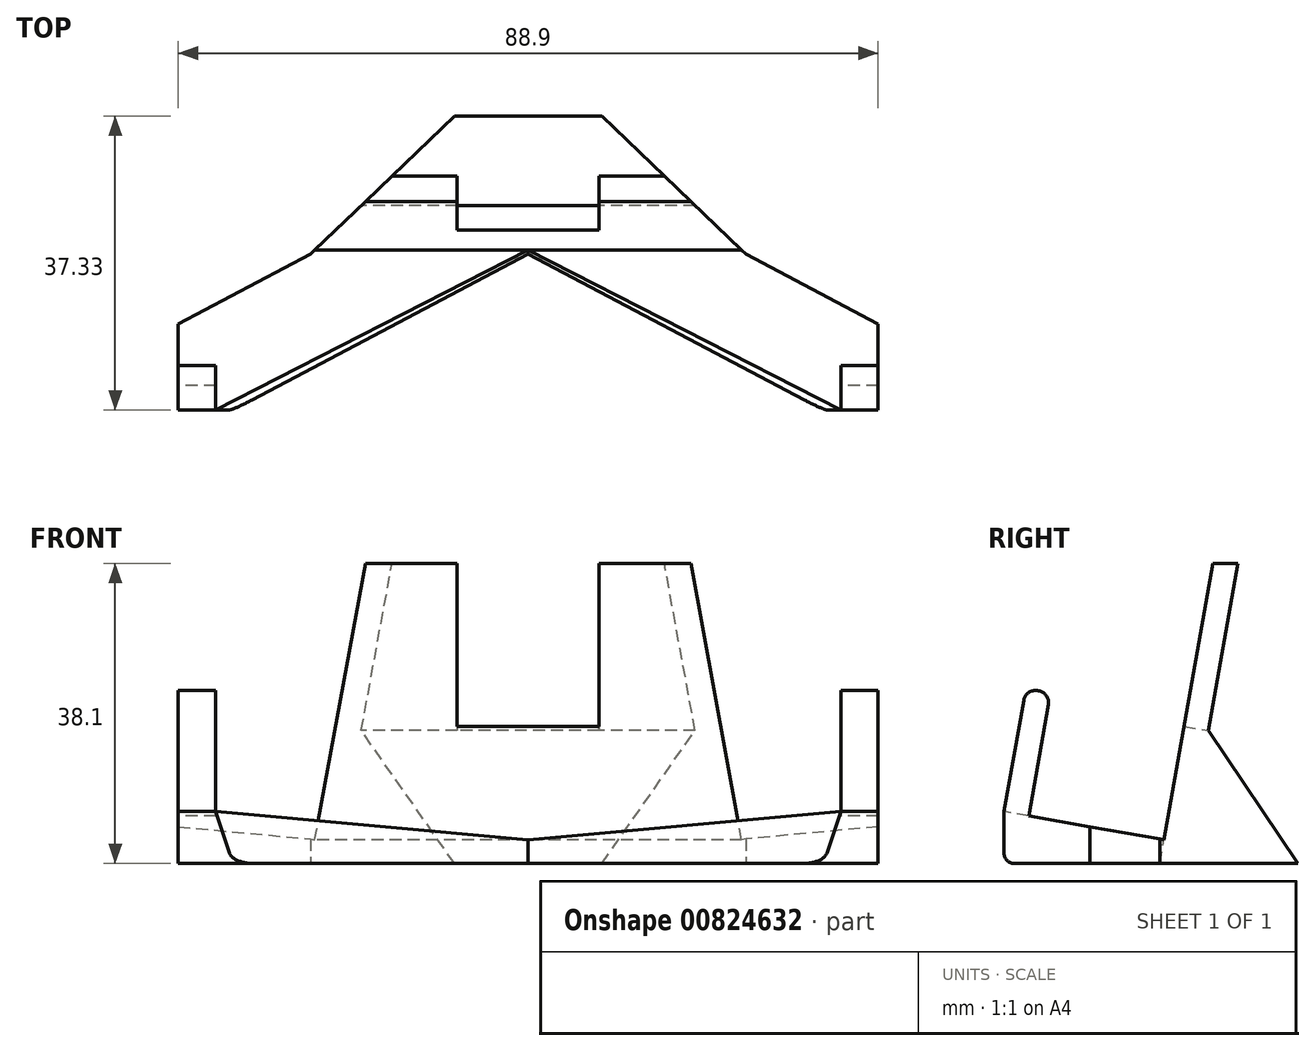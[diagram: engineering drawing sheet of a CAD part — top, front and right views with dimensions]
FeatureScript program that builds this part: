
annotation { "Feature Type Name" : "Feature", "Feature Type Description" : "" }
export const myFeature = defineFeature(function(context is Context, id is Id, definition is map)
    precondition{}
    {
        {
            var Q0;
            Q0=qCreatedBy(makeId("Front.planeOp"),FACE);
            var sketch = newSketch(context, id + "F0", { "sketchPlane" : qUnion([Q0])});
            skLineSegment(sketch, "E0.bottom", {"start": v(0, 0) * mm, "end": v(88.9, 0) * mm});
            skLineSegment(sketch, "E0.top", {"start": v(0, 38.1) * mm, "end": v(88.9, 38.1) * mm});
            skLineSegment(sketch, "E0.left", {"start": v(0, 0) * mm, "end": v(0, 38.1) * mm});
            skLineSegment(sketch, "E0.right", {"start": v(88.9, 0) * mm, "end": v(88.9, 38.1) * mm});
            skSolve(sketch);
        }
        {
            var Q0;
            Q0=makeQuery(id+"F0.imprint","IMPRINT",FACE,{"disambiguationData":[TD([[makeQuery(id+"F0.imprint","IMPRINT",EDGE,{"derivedFrom":sQuery(id+"F0.wireOp",EDGE,"E0.bottom")}),1.0]])]});
            extrude(context, id + "F1", {"entities" : qUnion([Q0]), "depth" : 42.85 * mm, "offsetDistance" : 25.4 * mm});
        }
        {
            var Q0;
            Q0=makeQuery(id+"F1.opExtrude","SWEPT_FACE",FACE,{"disambiguationData":[OSD([sQuery(id+"F0.wireOp",EDGE,"E0.left")])]});
            var sketch = newSketch(context, id + "F2", { "sketchPlane" : qUnion([Q0])});
            skLineSegment(sketch, "E1", {"start": v(22.54, 3) * mm, "end": v(39.72, 6.03) * mm});
            skLineSegment(sketch, "E2", {"start": v(42.85, 6.58) * mm, "end": v(40.1, 22.22) * mm});
            skLineSegment(sketch, "E3", {"start": v(39.72, 6.03) * mm, "end": v(36.97, 21.67) * mm});
            skLineSegment(sketch, "E4", {"start": v(36.97, 21.67) * mm, "end": v(40.1, 22.22) * mm});
            skLineSegment(sketch, "E5", {"start": v(16.35, 38.1) * mm, "end": v(22.54, 3) * mm});
            skLineSegment(sketch, "E6", {"start": v(13.13, 38.1) * mm, "end": v(16.87, 16.87) * mm});
            skLineSegment(sketch, "E7", {"start": v(16.87, 16.87) * mm, "end": v(5.52, 0) * mm});
            skPoint(sketch, "E8.start.orphan", {"position": v(23.8, 0) * mm});
            skSolve(sketch);
        }
        {
            var Q0;
            {var subQ4=sQuery(id+"F2.wireOp",EDGE,"E6");Q0=makeQuery(id+"F2.imprint","IMPRINT",FACE,{"disambiguationData":[TD([[makeQuery(id+"F2.imprint","IMPRINT",EDGE,{"derivedFrom":subQ4}),-1.0]])]});}
            var Q1;
            Q1=makeQuery(id+"F2.imprint","IMPRINT",FACE,{"disambiguationData":[TD([[makeQuery(id+"F2.imprint","IMPRINT",EDGE,{"derivedFrom":sQuery(id+"F2.wireOp",EDGE,"E1")}),1.0]])]});
            extrude(context, id + "F3", {"entities" : qUnion([Q0, Q1]), "operationType" : NewBodyOperationType.REMOVE, "oppositeDirection" : true, "depth" : 127 * mm, "offsetDistance" : 25.4 * mm});
        }
        {
            var Q0;
            Q0=makeQuery(id+"F3.boolean.opBoolean","COPY",FACE,{"derivedFrom":makeQuery(id+"F3.opExtrude","SWEPT_FACE",FACE,{"disambiguationData":[OSD([sQuery(id+"F2.wireOp",EDGE,"E2")])]})});
            var sketch = newSketch(context, id + "F4", { "sketchPlane" : qUnion([Q0])});
            skLineSegment(sketch, "E9.bottom", {"start": v(4.75, 14.92) * mm, "end": v(84.15, 14.92) * mm});
            skLineSegment(sketch, "E9.top", {"start": v(4.75, -0.96) * mm, "end": v(84.15, -0.96) * mm});
            skLineSegment(sketch, "E9.left", {"start": v(4.75, 14.92) * mm, "end": v(4.75, -0.96) * mm});
            skLineSegment(sketch, "E9.right", {"start": v(84.15, 14.92) * mm, "end": v(84.15, -0.96) * mm});
            skSolve(sketch);
        }
        {
            var Q0;
            Q0=makeQuery(id+"F4.imprint","IMPRINT",FACE,{"disambiguationData":[TD([[makeQuery(id+"F4.imprint","IMPRINT",EDGE,{"derivedFrom":sQuery(id+"F4.wireOp",EDGE,"E9.bottom")}),1.0]])]});
            extrude(context, id + "F5", {"entities" : qUnion([Q0]), "operationType" : NewBodyOperationType.REMOVE, "oppositeDirection" : true, "depth" : 6.35 * mm, "offsetDistance" : 25.4 * mm});
        }
        {
            var Q0;
            Q0=makeQuery(id+"F5.boolean.opBoolean","MERGE",FACE,{"derivedFrom":[makeQuery(id+"F3.boolean.opBoolean","COPY",FACE,{"derivedFrom":makeQuery(id+"F3.opExtrude","SWEPT_FACE",FACE,{"disambiguationData":[OSD([sQuery(id+"F2.wireOp",EDGE,"E1")])]})}),makeQuery(id+"F5.opExtrude","SWEPT_FACE",FACE,{"disambiguationData":[OSD([sQuery(id+"F4.wireOp",EDGE,"E9.top")])]})]});
            var sketch = newSketch(context, id + "F6", { "sketchPlane" : qUnion([Q0])});
            skLineSegment(sketch, "E10", {"start": v(0, -22.72) * mm, "end": v(88.9, -22.72) * mm});
            skLineSegment(sketch, "E11", {"start": v(4.75, -43.34) * mm, "end": v(44.45, -22.72) * mm});
            skLineSegment(sketch, "E12", {"start": v(84.15, -43.34) * mm, "end": v(44.45, -22.72) * mm});
            skLineSegment(sketch, "E13", {"start": v(0, -31.44) * mm, "end": v(16.8, -22.72) * mm});
            skLineSegment(sketch, "E14", {"start": v(88.9, -31.44) * mm, "end": v(72.1, -22.72) * mm});
            skSolve(sketch);
        }
        {
            var Q0;
            {var subQ3=sQuery(id+"F6.wireOp",EDGE,"E13");Q0=makeQuery(id+"F6.imprint","IMPRINT",FACE,{"disambiguationData":[TD([[makeQuery(id+"F6.imprint","IMPRINT",EDGE,{"derivedFrom":subQ3}),1.0]])]});}
            var Q1;
            Q1=makeQuery(id+"F6.imprint","IMPRINT",FACE,{"disambiguationData":[TD([[makeQuery(id+"F6.imprint","IMPRINT",EDGE,{"derivedFrom":sQuery(id+"F6.wireOp",EDGE,"E11")}),-1.0]])]});
            var Q2;
            {var subQ3=sQuery(id+"F6.wireOp",EDGE,"E14");Q2=makeQuery(id+"F6.imprint","IMPRINT",FACE,{"disambiguationData":[TD([[makeQuery(id+"F6.imprint","IMPRINT",EDGE,{"derivedFrom":subQ3}),-1.0]])]});}
            extrude(context, id + "F7", {"entities" : qUnion([Q0, Q1, Q2]), "operationType" : NewBodyOperationType.REMOVE, "oppositeDirection" : true, "depth" : 25.4 * mm, "offsetDistance" : 25.4 * mm});
        }
        {
            var Q0;
            Q0=makeQuery(id+"F1.opExtrude","SWEPT_FACE",FACE,{"disambiguationData":[OSD([sQuery(id+"F0.wireOp",EDGE,"E0.bottom")])]});
            var sketch = newSketch(context, id + "F8", { "sketchPlane" : qUnion([Q0])});
            skLineSegment(sketch, "E15", {"start": v(44.45, 5.52) * mm, "end": v(44.45, -5.42) * mm});
            skPoint(sketch, "E15.endSnap0", {"position": v(44.45, 5.52) * mm});
            skLineSegment(sketch, "E16", {"start": v(16.8, 23.07) * mm, "end": v(35.08, 5.52) * mm});
            skLineSegment(sketch, "E17", {"start": v(72.1, 23.07) * mm, "end": v(53.82, 5.52) * mm});
            skPoint(sketch, "E18.start.orphan", {"position": v(25.7, 32.96) * mm});
            skPoint(sketch, "E19.start.orphan", {"position": v(63.2, 32.96) * mm});
            skSolve(sketch);
        }
        {
            var Q0;
            {var subQ0=sQuery(id+"F8.wireOp",EDGE,"E16");Q0=makeQuery(id+"F8.imprint","IMPRINT",FACE,{"disambiguationData":[TD([[makeQuery(id+"F8.imprint","IMPRINT",EDGE,{"derivedFrom":subQ0}),-1.0]])]});}
            var Q1;
            {var subQ0=sQuery(id+"F8.wireOp",EDGE,"E17");Q1=makeQuery(id+"F8.imprint","IMPRINT",FACE,{"disambiguationData":[TD([[makeQuery(id+"F8.imprint","IMPRINT",EDGE,{"derivedFrom":subQ0}),1.0]])]});}
            extrude(context, id + "F9", {"entities" : qUnion([Q0, Q1]), "operationType" : NewBodyOperationType.REMOVE, "oppositeDirection" : true, "depth" : 127 * mm, "offsetDistance" : 25.4 * mm});
        }
        {
            var Q0;
            Q0=makeQuery(id+"F3.boolean.opBoolean","COPY",EDGE,{"derivedFrom":makeQuery(id+"F3.opExtrude","SWEPT_EDGE",EDGE,{"disambiguationData":[OSD([sQuery(id+"F0.wireOp",EDGE,"E0.top"),sQuery(id+"F0.wireOp",EDGE,"E0.left"),sQuery(id+"F2.wireOp",EDGE,"E6")])]})});
            var Q1;
            Q1=makeQuery(id+"F3.boolean.opBoolean","COPY",EDGE,{"derivedFrom":makeQuery(id+"F3.opExtrude","SWEPT_EDGE",EDGE,{"disambiguationData":[OSD([sQuery(id+"F0.wireOp",EDGE,"E0.top"),sQuery(id+"F0.wireOp",EDGE,"E0.left"),sQuery(id+"F2.wireOp",EDGE,"E5")])]})});
            var Q2;
            {var subQ0=sQuery(id+"F2.wireOp",EDGE,"E3");var subQ1=sQuery(id+"F2.wireOp",EDGE,"E4");Q2=makeQuery(id+"F5.boolean.opBoolean","SPLIT",EDGE,{"disambiguationData":[TD([makeQuery(id+"F1.opExtrude","SWEPT_FACE",FACE,{"disambiguationData":[OSD([sQuery(id+"F0.wireOp",EDGE,"E0.left")])]})])],"derivedFrom":makeQuery(id+"F3.boolean.opBoolean","COPY",EDGE,{"derivedFrom":makeQuery(id+"F3.opExtrude","SWEPT_EDGE",EDGE,{"disambiguationData":[OSD([subQ0,subQ1])]})})});}
            var Q3;
            {var subQ0=sQuery(id+"F2.wireOp",EDGE,"E2");var subQ1=sQuery(id+"F2.wireOp",EDGE,"E4");Q3=makeQuery(id+"F5.boolean.opBoolean","SPLIT",EDGE,{"disambiguationData":[TD([makeQuery(id+"F1.opExtrude","SWEPT_FACE",FACE,{"disambiguationData":[OSD([sQuery(id+"F0.wireOp",EDGE,"E0.left")])]})])],"derivedFrom":makeQuery(id+"F3.boolean.opBoolean","COPY",EDGE,{"derivedFrom":makeQuery(id+"F3.opExtrude","SWEPT_EDGE",EDGE,{"disambiguationData":[OSD([subQ0,subQ1])]})})});}
            var Q4;
            {var subQ0=sQuery(id+"F2.wireOp",EDGE,"E3");var subQ1=sQuery(id+"F2.wireOp",EDGE,"E4");Q4=makeQuery(id+"F5.boolean.opBoolean","SPLIT",EDGE,{"disambiguationData":[TD([makeQuery(id+"F1.opExtrude","SWEPT_FACE",FACE,{"disambiguationData":[OSD([sQuery(id+"F0.wireOp",EDGE,"E0.right")])]})])],"derivedFrom":makeQuery(id+"F3.boolean.opBoolean","COPY",EDGE,{"derivedFrom":makeQuery(id+"F3.opExtrude","SWEPT_EDGE",EDGE,{"disambiguationData":[OSD([subQ0,subQ1])]})})});}
            var Q5;
            {var subQ0=sQuery(id+"F2.wireOp",EDGE,"E2");var subQ1=sQuery(id+"F2.wireOp",EDGE,"E4");Q5=makeQuery(id+"F5.boolean.opBoolean","SPLIT",EDGE,{"disambiguationData":[TD([makeQuery(id+"F1.opExtrude","SWEPT_FACE",FACE,{"disambiguationData":[OSD([sQuery(id+"F0.wireOp",EDGE,"E0.right")])]})])],"derivedFrom":makeQuery(id+"F3.boolean.opBoolean","COPY",EDGE,{"derivedFrom":makeQuery(id+"F3.opExtrude","SWEPT_EDGE",EDGE,{"disambiguationData":[OSD([subQ0,subQ1])]})})});}
            fillet(context, id + "F10", {"entities" : qUnion([Q0, Q1, Q2, Q3, Q4, Q5]), "radius" : 1.52 * mm, "tangentPropagation" : true, "allowEdgeOverflow" : false});
        }
        {
            var Q0;
            Q0=makeQuery(id+"F1.opExtrude","SWEPT_FACE",FACE,{"disambiguationData":[OSD([sQuery(id+"F0.wireOp",EDGE,"E0.bottom")])]});
            var sketch = newSketch(context, id + "F11", { "sketchPlane" : qUnion([Q0])});
            skLineSegment(sketch, "E20", {"start": v(0, 31.93) * mm, "end": v(16.8, 23.07) * mm});
            skLineSegment(sketch, "E21", {"start": v(16.8, 23.07) * mm, "end": v(16.1, 21.75) * mm});
            skLineSegment(sketch, "E22", {"start": v(16.1, 21.75) * mm, "end": v(0, 30.78) * mm});
            skLineSegment(sketch, "E23", {"start": v(0, 30.78) * mm, "end": v(0, 31.93) * mm});
            skLineSegment(sketch, "E24", {"start": v(72.1, 23.07) * mm, "end": v(72.6, 22.13) * mm});
            skLineSegment(sketch, "E25", {"start": v(72.6, 22.13) * mm, "end": v(88.9, 30.41) * mm});
            skLineSegment(sketch, "E26", {"start": v(88.9, 30.41) * mm, "end": v(88.9, 31.93) * mm});
            skLineSegment(sketch, "E27", {"start": v(88.9, 31.93) * mm, "end": v(72.1, 23.07) * mm});
            skSolve(sketch);
        }
        {
            var Q0;
            Q0=makeQuery(id+"F11.imprint","IMPRINT",FACE,{"disambiguationData":[TD([[makeQuery(id+"F11.imprint","IMPRINT",EDGE,{"derivedFrom":sQuery(id+"F11.wireOp",EDGE,"E20")}),-1.0]])]});
            var Q1;
            Q1=makeQuery(id+"F11.imprint","IMPRINT",FACE,{"disambiguationData":[TD([[makeQuery(id+"F11.imprint","IMPRINT",EDGE,{"derivedFrom":sQuery(id+"F11.wireOp",EDGE,"E24")}),1.0]])]});
            extrude(context, id + "F12", {"entities" : qUnion([Q0, Q1]), "operationType" : NewBodyOperationType.REMOVE, "oppositeDirection" : true, "depth" : 25.4 * mm, "offsetDistance" : 25.4 * mm});
        }
        {
            var Q0;
            Q0=makeQuery(id+"F3.boolean.opBoolean","COPY",EDGE,{"derivedFrom":makeQuery(id+"F3.opExtrude","SWEPT_EDGE",EDGE,{"disambiguationData":[OSD([sQuery(id+"F0.wireOp",EDGE,"E0.bottom"),sQuery(id+"F0.wireOp",EDGE,"E0.left"),sQuery(id+"F2.wireOp",EDGE,"E7")])]})});
            var Q1;
            {var subQ0=sQuery(id+"F0.wireOp",EDGE,"E0.bottom");var subQ1=sQuery(id+"F0.wireOp",EDGE,"E0.right");Q1=makeQuery(id+"F7.boolean.opBoolean","SPLIT",EDGE,{"disambiguationData":[TD([makeQuery(id+"F1.opExtrude","SWEPT_FACE",FACE,{"disambiguationData":[OSD([subQ1])]})])],"derivedFrom":makeQuery(id+"F1.opExtrude","CAP_EDGE",EDGE,{"disambiguationData":[OSD([subQ0])],"isStart":false})});}
            var Q2;
            {var subQ0=sQuery(id+"F0.wireOp",EDGE,"E0.bottom");var subQ1=sQuery(id+"F0.wireOp",EDGE,"E0.left");Q2=makeQuery(id+"F7.boolean.opBoolean","SPLIT",EDGE,{"disambiguationData":[TD([makeQuery(id+"F1.opExtrude","SWEPT_FACE",FACE,{"disambiguationData":[OSD([subQ1])]})])],"derivedFrom":makeQuery(id+"F1.opExtrude","CAP_EDGE",EDGE,{"disambiguationData":[OSD([subQ0])],"isStart":false})});}
            fillet(context, id + "F13", {"entities" : qUnion([Q0, Q1, Q2]), "radius" : 1.27 * mm, "tangentPropagation" : true, "allowEdgeOverflow" : false});
        }
        {
            var Q0;
            Q0=makeQuery(id+"F3.boolean.opBoolean","COPY",FACE,{"derivedFrom":makeQuery(id+"F3.opExtrude","SWEPT_FACE",FACE,{"disambiguationData":[OSD([sQuery(id+"F2.wireOp",EDGE,"E6")])]})});
            var sketch = newSketch(context, id + "F14", { "sketchPlane" : qUnion([Q0])});
            skLineSegment(sketch, "E28", {"start": v(-65.65, 13.68) * mm, "end": v(-53.46, 13.68) * mm});
            skLineSegment(sketch, "E29", {"start": v(-23.25, 13.68) * mm, "end": v(-35.44, 13.68) * mm});
            skLineSegment(sketch, "E30", {"start": v(-53.46, 13.68) * mm, "end": v(-53.46, 39.56) * mm});
            skLineSegment(sketch, "E31", {"start": v(-53.46, 39.56) * mm, "end": v(-35.44, 39.56) * mm});
            skLineSegment(sketch, "E32", {"start": v(-35.44, 39.56) * mm, "end": v(-35.44, 13.68) * mm});
            skSolve(sketch);
        }
        {
            var Q0;
            {var subQ0=sQuery(id+"F14.wireOp",EDGE,"E30");var subQ1=sQuery(id+"F2.wireOp",EDGE,"E6");var subQ2=makeQuery(id+"F3.boolean.opBoolean","COPY",EDGE,{"derivedFrom":makeQuery(id+"F3.opExtrude","SWEPT_EDGE",EDGE,{"disambiguationData":[OSD([subQ1,sQuery(id+"F2.wireOp",EDGE,"E7")])]})});var subQ3=makeQuery(id+"F14.imprint","INTERSECT",VERTEX,{"derivedFrom":[subQ2,sQuery(id+"F14.wireOp",EDGE,"E28"),subQ0]});Q0=makeQuery(id+"F14.imprint","IMPRINT",FACE,{"disambiguationData":[TD([[makeQuery(id+"F14.imprint","IMPRINT",EDGE,{"disambiguationData":[TD([[subQ3,-1.0]])],"derivedFrom":subQ0}),-1.0]])]});}
            var Q1;
            {var subQ0=sQuery(id+"F14.wireOp",EDGE,"E31");Q1=makeQuery(id+"F14.imprint","IMPRINT",FACE,{"disambiguationData":[TD([[makeQuery(id+"F14.imprint","IMPRINT",EDGE,{"derivedFrom":subQ0}),-1.0]])]});}
            extrude(context, id + "F15", {"entities" : qUnion([Q0, Q1]), "operationType" : NewBodyOperationType.REMOVE, "oppositeDirection" : true, "depth" : 25.4 * mm, "offsetDistance" : 25.4 * mm});
        }
    });
